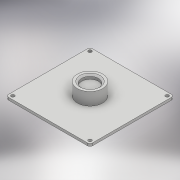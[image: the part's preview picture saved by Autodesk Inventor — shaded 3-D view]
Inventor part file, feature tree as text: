
AUTODESK INVENTOR PART (.ipt)
format: ipt  version: 2017 (Build 210142000, 142)  size: 142,336 bytes
history: native  units: mm
features: extrude x3, sketch x1, chamfer x1
ambient origin geometry x8: Origin, YZ Plane, XZ Plane, XY Plane, X Axis, Y Axis, Z Axis, Center Point
bodies: Solid1 (feature_tree)
feature tree (5):
  sketch  "Sketch1"  dims[d0=100.0mm d1=100.0mm d2=4.0mm d3=3.0mm d4=4.0mm d5=20.0mm d6=30.0mm d7=3.0mm d8=0.0mm d9=15.0mm d10=0.0mm d11=10.0mm d12=0.0mm d13=2.0mm d14=2.0mm d15=45.0deg]
  extrude  "Extrusion1"  Depth=100.0mm
  extrude  "Extrusion2"  Depth=2.0mm
  extrude  "Extrusion3"  Depth=3.0mm
  chamfer  "Chamfer1"  Distance=4.0mm
